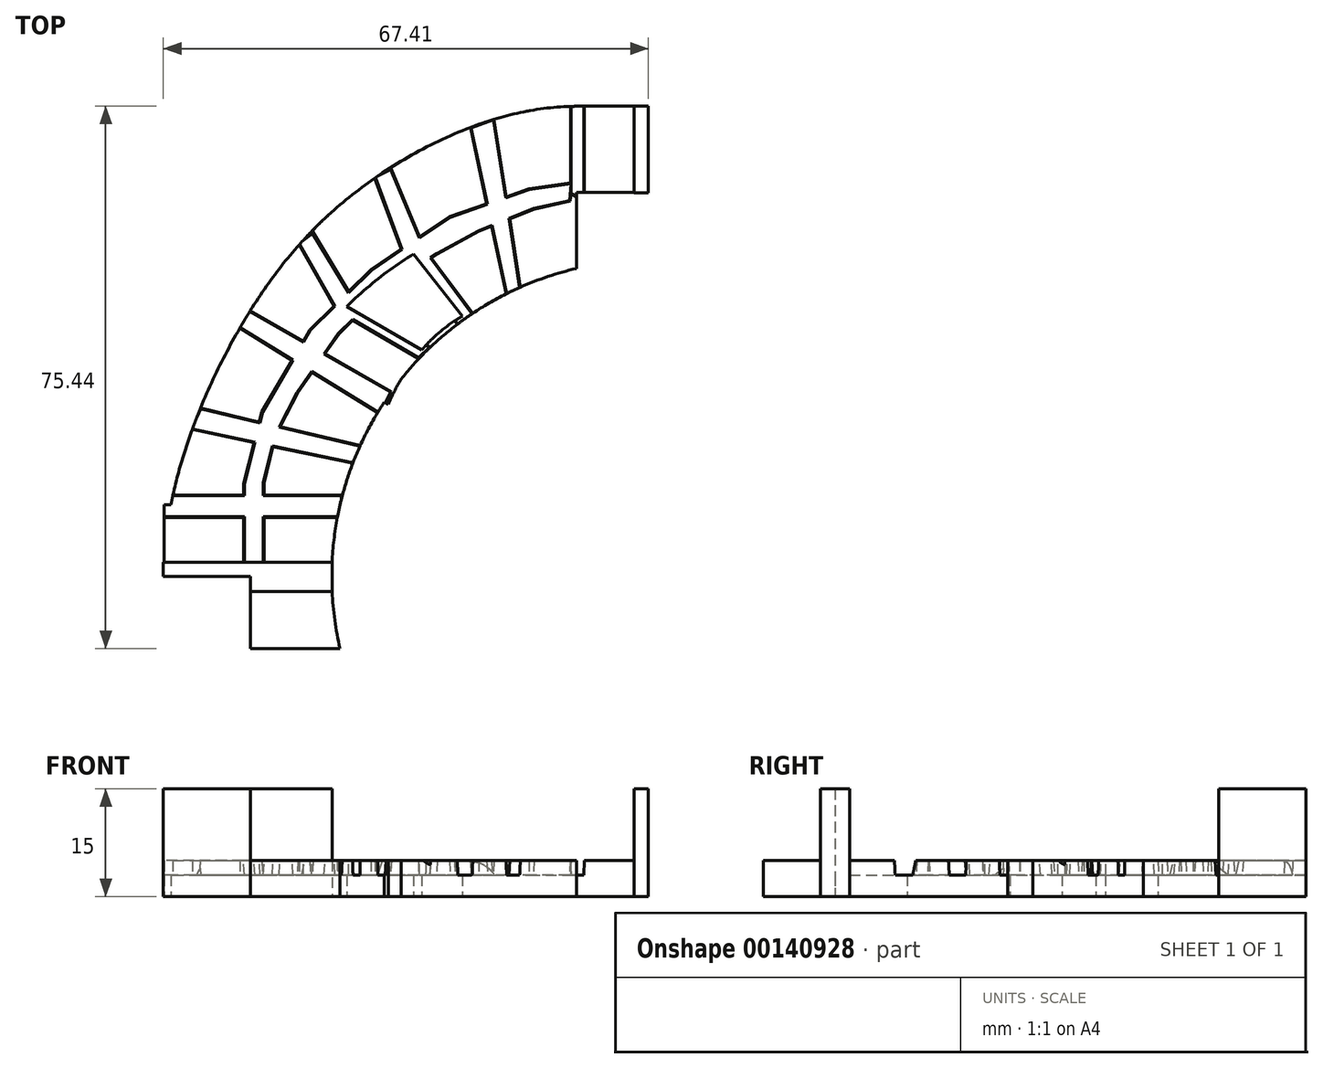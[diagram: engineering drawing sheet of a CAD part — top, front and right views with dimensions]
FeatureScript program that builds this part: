
annotation { "Feature Type Name" : "Feature", "Feature Type Description" : "" }
export const myFeature = defineFeature(function(context is Context, id is Id, definition is map)
    precondition{}
    {
        {
            var Q0;
            Q0=qCreatedBy(makeId("Top.planeOp"),FACE);
            var sketch = newSketch(context, id + "F0", { "sketchPlane" : qUnion([Q0])});
            skLineSegment(sketch, "E0", {"start": v(-44, 0) * mm, "end": v(-55.3, 0) * mm});
            skLineSegment(sketch, "E1.bottom", {"start": v(-55.3, 0) * mm, "end": v(-44, 0) * mm});
            skLineSegment(sketch, "E1.top", {"start": v(-55.3, 10) * mm, "end": v(-42.85, 10) * mm});
            skLineSegment(sketch, "E1.left", {"start": v(-55.3, 0) * mm, "end": v(-55.3, 10) * mm});
            skLineSegment(sketch, "E1.right", {"start": v(-40, 0) * mm, "end": v(-40, 0) * mm});
            skLineSegment(sketch, "E2.bottom", {"start": v(0, 53.4) * mm, "end": v(-10, 53.4) * mm});
            skLineSegment(sketch, "E2.right", {"start": v(-10, 53.4) * mm, "end": v(-10, 42.85) * mm});
            skLineSegment(sketch, "E3.bottom", {"start": v(-55.3, 10) * mm, "end": v(-67.3, 10) * mm});
            skLineSegment(sketch, "E3.top", {"start": v(-55.3, 0) * mm, "end": v(-67.3, 0) * mm});
            skLineSegment(sketch, "E3.left", {"start": v(-55.3, 10) * mm, "end": v(-55.3, 0) * mm});
            skLineSegment(sketch, "E3.right", {"start": v(-67.3, 10) * mm, "end": v(-67.3, 0) * mm});
            skLineSegment(sketch, "E4.bottom", {"start": v(-10, 53.4) * mm, "end": v(0, 53.4) * mm});
            skLineSegment(sketch, "E4.top", {"start": v(-10, 65.4) * mm, "end": v(0, 65.4) * mm});
            skLineSegment(sketch, "E4.left", {"start": v(-10, 53.4) * mm, "end": v(-10, 65.4) * mm});
            skLineSegment(sketch, "E4.right", {"start": v(0, 53.4) * mm, "end": v(0, 65.4) * mm});
            skFitSpline(sketch, "E5", {"points": [v(-67.3, 0) * mm, v(-56.1, 35.7) * mm, v(-37.14, 56.01) * mm, v(-10, 65.4) * mm], "startDerivative": vector(-1.94, 97.4) * mm, "endDerivative": vector(89.19, 0.31) * mm});
            skFitSpline(sketch, "E6", {"points": [v(-55.3, 10) * mm, v(-43.15, 36.3) * mm, v(-25.7, 48.72) * mm, v(-10, 53.4) * mm], "startDerivative": vector(1.43, 78.12) * mm, "endDerivative": vector(52.36, -0.95) * mm});
            skLineSegment(sketch, "E7", {"start": v(-20.71, 51) * mm, "end": v(-18.75, 39.8) * mm});
            skLineSegment(sketch, "E8", {"start": v(-25.83, 36.23) * mm, "end": v(-32.62, 44.89) * mm});
            skLineSegment(sketch, "E9", {"start": v(-31.47, 31.55) * mm, "end": v(-41.92, 37.56) * mm});
            skLineSegment(sketch, "E10", {"start": v(-47.77, 30.64) * mm, "end": v(-36.16, 23.96) * mm});
            skLineSegment(sketch, "E11", {"start": v(-40.58, 17) * mm, "end": v(-55.12, 19.97) * mm});
            skLineSegment(sketch, "E12", {"start": v(-20.71, 51) * mm, "end": v(-22.71, 63.18) * mm});
            skLineSegment(sketch, "E13", {"start": v(-55.12, 19.97) * mm, "end": v(-62.99, 21.58) * mm});
            skLineSegment(sketch, "E14", {"start": v(-47.77, 30.64) * mm, "end": v(-56.1, 35.7) * mm});
            skLineSegment(sketch, "E15", {"start": v(-32.62, 44.89) * mm, "end": v(-37.14, 56.01) * mm});
            skLineSegment(sketch, "E16", {"start": v(-41.92, 37.56) * mm, "end": v(-47.65, 47.1) * mm});
            skLineSegment(sketch, "E17.bottom", {"start": v(-67.3, 0) * mm, "end": v(-44, 0) * mm});
            skLineSegment(sketch, "E17.top", {"start": v(-67.3, 2) * mm, "end": v(-43.95, 2) * mm});
            skLineSegment(sketch, "E17.left", {"start": v(-67.3, 0) * mm, "end": v(-67.3, 2) * mm});
            skLineSegment(sketch, "E18.top", {"start": v(-55.3, -2) * mm, "end": v(-43.95, -2) * mm});
            skLineSegment(sketch, "E19.top", {"start": v(-55.3, -10) * mm, "end": v(-42.85, -10) * mm});
            skLineSegment(sketch, "E19.left", {"start": v(-55.3, 0) * mm, "end": v(-55.3, -10) * mm});
            skLineSegment(sketch, "E20.bottom", {"start": v(0, 65.4) * mm, "end": v(-2, 65.4) * mm});
            skLineSegment(sketch, "E20.left", {"start": v(0, 65.4) * mm, "end": v(0, 53.4) * mm});
            skLineSegment(sketch, "E20.right", {"start": v(-2, 65.4) * mm, "end": v(-2, 53.4) * mm});
            skPoint(sketch, "E21.top.end.orphan", {"position": v(2, 40) * mm});
            skPoint(sketch, "E22", {"position": v(-55.3, -2) * mm});
            skArc(sketch, "E23", {"start": v(-10, 42.85) * mm, "mid": v(-37.37, 23.23) * mm, "end": v(-42.85, -10) * mm});
            skFitSpline(sketch, "E24.trimOffspring", {"points": [v(-40, 0) * mm, v(-37.14, 21.48) * mm, v(-25.7, 36.3) * mm, v(0, 40) * mm], "startDerivative": vector(0, 72.34) * mm, "endDerivative": vector(82.88, 0) * mm});
            skLineSegment(sketch, "E25.trimOffspring", {"start": v(-40, 0) * mm, "end": v(-39.99, 0) * mm});
            skPoint(sketch, "E26.orphan", {"position": v(-39.99, -2) * mm});
            skPoint(sketch, "E27.orphan", {"position": v(-39.99, -10) * mm});
            skSolve(sketch);
        }
        {
            var Q0;
            Q0=qCreatedBy(makeId("Top.planeOp"),FACE);
            cPlane(context, id + "F1", {"entities" : qUnion([Q0]), "cplaneType" : CPlaneType.OFFSET, "offset" : 3 * mm, "width" : 150 * mm, "height" : 150 * mm});
        }
        {
            var Q0;
            Q0=qCreatedBy(id+"F1.planeOp",FACE);
            var sketch = newSketch(context, id + "F2", { "sketchPlane" : qUnion([Q0])});
            skLineSegment(sketch, "E28.bottom", {"start": v(-67.6, 8.33) * mm, "end": v(-42.66, 8.33) * mm});
            skLineSegment(sketch, "E28.top", {"start": v(-67.6, 11.24) * mm, "end": v(-42.66, 11.24) * mm});
            skLineSegment(sketch, "E28.left", {"start": v(-67.6, 8.33) * mm, "end": v(-67.6, 11.24) * mm});
            skLineSegment(sketch, "E28.right", {"start": v(-42.66, 8.33) * mm, "end": v(-42.66, 11.24) * mm});
            skLineSegment(sketch, "E29", {"start": v(-63.47, 20.57) * mm, "end": v(-40.98, 15.83) * mm});
            skLineSegment(sketch, "E30", {"start": v(-40.98, 15.83) * mm, "end": v(-40.06, 18.12) * mm});
            skLineSegment(sketch, "E31", {"start": v(-40.06, 18.12) * mm, "end": v(-62.25, 23.32) * mm});
            skLineSegment(sketch, "E32", {"start": v(-62.25, 23.32) * mm, "end": v(-63.47, 20.57) * mm});
            skLineSegment(sketch, "E33", {"start": v(-56.77, 34.65) * mm, "end": v(-37.27, 22.7) * mm});
            skLineSegment(sketch, "E34", {"start": v(-37.27, 22.7) * mm, "end": v(-35.84, 25.66) * mm});
            skLineSegment(sketch, "E35", {"start": v(-35.84, 25.66) * mm, "end": v(-55.45, 36.9) * mm});
            skLineSegment(sketch, "E36", {"start": v(-55.45, 36.9) * mm, "end": v(-56.77, 34.65) * mm});
            skLineSegment(sketch, "E37", {"start": v(-48.5, 46.29) * mm, "end": v(-43.2, 37) * mm});
            skLineSegment(sketch, "E38", {"start": v(-43.2, 37) * mm, "end": v(-31.96, 30.46) * mm});
            skLineSegment(sketch, "E39", {"start": v(-31.96, 30.46) * mm, "end": v(-30.43, 31.9) * mm});
            skLineSegment(sketch, "E40", {"start": v(-30.43, 31.9) * mm, "end": v(-40.74, 37.92) * mm});
            skLineSegment(sketch, "E41", {"start": v(-40.74, 37.92) * mm, "end": v(-46.66, 47.72) * mm});
            skLineSegment(sketch, "E42", {"start": v(-46.66, 47.72) * mm, "end": v(-48.5, 46.29) * mm});
            skLineSegment(sketch, "E43", {"start": v(-37.94, 55.53) * mm, "end": v(-33.73, 44.18) * mm});
            skLineSegment(sketch, "E44", {"start": v(-33.73, 44.18) * mm, "end": v(-26.43, 35.1) * mm});
            skLineSegment(sketch, "E45", {"start": v(-26.43, 35.1) * mm, "end": v(-24.49, 36.56) * mm});
            skLineSegment(sketch, "E46", {"start": v(-24.49, 36.56) * mm, "end": v(-31.14, 45.43) * mm});
            skLineSegment(sketch, "E47", {"start": v(-31.14, 45.43) * mm, "end": v(-35.84, 56.58) * mm});
            skLineSegment(sketch, "E48", {"start": v(-35.84, 56.58) * mm, "end": v(-37.94, 55.53) * mm});
            skLineSegment(sketch, "E49", {"start": v(-19.63, 39.08) * mm, "end": v(-24.61, 62.41) * mm});
            skLineSegment(sketch, "E50", {"start": v(-24.61, 62.41) * mm, "end": v(-21.55, 63.54) * mm});
            skLineSegment(sketch, "E51", {"start": v(-21.55, 63.54) * mm, "end": v(-17.87, 40.15) * mm});
            skLineSegment(sketch, "E52", {"start": v(-17.87, 40.15) * mm, "end": v(-19.63, 39.08) * mm});
            skLineSegment(sketch, "E53", {"start": v(-10.72, 53.32) * mm, "end": v(-10.72, 65.48) * mm});
            skLineSegment(sketch, "E54", {"start": v(-10.72, 65.48) * mm, "end": v(-8.99, 65.48) * mm});
            skLineSegment(sketch, "E55", {"start": v(-8.99, 65.48) * mm, "end": v(-8.99, 52.4) * mm});
            skLineSegment(sketch, "E56", {"start": v(-8.99, 52.4) * mm, "end": v(-10.72, 53.32) * mm});
            skLineSegment(sketch, "E57", {"start": v(-56.17, 0) * mm, "end": v(-56.17, 12.88) * mm});
            skLineSegment(sketch, "E58", {"start": v(-56.17, 12.88) * mm, "end": v(-53.61, 22.9) * mm});
            skLineSegment(sketch, "E59", {"start": v(-53.61, 22.9) * mm, "end": v(-46.98, 34.23) * mm});
            skLineSegment(sketch, "E60", {"start": v(-46.98, 34.23) * mm, "end": v(-38.5, 42.6) * mm});
            skLineSegment(sketch, "E61", {"start": v(-38.5, 42.6) * mm, "end": v(-27.57, 49.95) * mm});
            skLineSegment(sketch, "E62", {"start": v(-27.57, 49.95) * mm, "end": v(-16.54, 53.83) * mm});
            skLineSegment(sketch, "E63", {"start": v(-16.54, 53.83) * mm, "end": v(-10.72, 54.65) * mm});
            skLineSegment(sketch, "E64", {"start": v(-10.72, 54.65) * mm, "end": v(-10.93, 52.3) * mm});
            skLineSegment(sketch, "E65", {"start": v(-10.93, 52.3) * mm, "end": v(-15.93, 51.18) * mm});
            skLineSegment(sketch, "E66", {"start": v(-15.93, 51.18) * mm, "end": v(-23.6, 48.12) * mm});
            skLineSegment(sketch, "E67", {"start": v(-23.6, 48.12) * mm, "end": v(-29.41, 44.95) * mm});
            skLineSegment(sketch, "E68", {"start": v(-29.41, 44.95) * mm, "end": v(-36.46, 40.25) * mm});
            skLineSegment(sketch, "E69", {"start": v(-36.46, 40.25) * mm, "end": v(-43.1, 33.82) * mm});
            skLineSegment(sketch, "E70", {"start": v(-43.1, 33.82) * mm, "end": v(-48.81, 25.65) * mm});
            skLineSegment(sketch, "E71", {"start": v(-48.81, 25.65) * mm, "end": v(-51.88, 19.73) * mm});
            skLineSegment(sketch, "E72", {"start": v(-51.88, 19.73) * mm, "end": v(-53.51, 13.09) * mm});
            skLineSegment(sketch, "E73", {"start": v(-53.51, 13.09) * mm, "end": v(-53.51, 0) * mm});
            skLineSegment(sketch, "E74", {"start": v(-53.51, 0) * mm, "end": v(-56.17, 0) * mm});
            skSolve(sketch);
        }
        {
            var Q0;
            Q0 = qSketchRegion(id + "F0", true);
            var Q1;
            {var subQ0=sQuery(id+"F0.wireOp",EDGE,"E3.bottom");Q1=makeQuery(id+"F0.imprint","IMPRINT",FACE,{"disambiguationData":[TD([[makeQuery(id+"F0.imprint","IMPRINT",EDGE,{"derivedFrom":subQ0}),1.0]])]});}
            var Q2;
            {var subQ0=sQuery(id+"F0.wireOp",EDGE,"E1.top");Q2=makeQuery(id+"F0.imprint","IMPRINT",FACE,{"disambiguationData":[TD([[makeQuery(id+"F0.imprint","IMPRINT",EDGE,{"derivedFrom":subQ0}),-1.0]])]});}
            extrude(context, id + "F3", {"entities" : qUnion([Q0, Q1, Q2]), "depth" : 5 * mm});
        }
        {
            var Q0;
            Q0 = qSketchRegion(id + "F2", true);
            extrude(context, id + "F4", {"entities" : qUnion([Q0]), "operationType" : NewBodyOperationType.REMOVE, "depth" : 25 * mm, "hasDraft" : true, "draftAngle" : 3 * degree});
        }
        {
            var Q0;
            Q0=qCreatedBy(makeId("Top.planeOp"),FACE);
            var sketch = newSketch(context, id + "F5", { "sketchPlane" : qUnion([Q0])});
            skLineSegment(sketch, "E75.bottom", {"start": v(0, 65.44) * mm, "end": v(-1.96, 65.44) * mm});
            skLineSegment(sketch, "E75.top", {"start": v(0, 53.34) * mm, "end": v(-1.96, 53.34) * mm});
            skLineSegment(sketch, "E75.left", {"start": v(0, 65.44) * mm, "end": v(0, 53.34) * mm});
            skLineSegment(sketch, "E75.right", {"start": v(-1.96, 65.44) * mm, "end": v(-1.96, 53.34) * mm});
            skLineSegment(sketch, "E76.bottom", {"start": v(-67.4, 0) * mm, "end": v(-43.92, 0) * mm});
            skLineSegment(sketch, "E76.top", {"start": v(-67.4, 1.98) * mm, "end": v(-43.92, 1.98) * mm});
            skLineSegment(sketch, "E76.left", {"start": v(-67.4, 0) * mm, "end": v(-67.4, 1.98) * mm});
            skLineSegment(sketch, "E76.right", {"start": v(-43.92, 0) * mm, "end": v(-43.92, 1.98) * mm});
            skLineSegment(sketch, "E77.bottom", {"start": v(-55.3, 0) * mm, "end": v(-43.92, 0) * mm});
            skLineSegment(sketch, "E77.top", {"start": v(-55.3, -2.07) * mm, "end": v(-43.92, -2.07) * mm});
            skLineSegment(sketch, "E77.right", {"start": v(-43.92, 0) * mm, "end": v(-43.92, -2.07) * mm});
            skLineSegment(sketch, "E78", {"start": v(-55.3, 0) * mm, "end": v(-55.3, -2.07) * mm});
            skPoint(sketch, "E79.orphan", {"position": v(-55.67, 0) * mm});
            skSolve(sketch);
        }
        {
            var Q0;
            Q0 = qSketchRegion(id + "F5", true);
            extrude(context, id + "F6", {"entities" : qUnion([Q0]), "operationType" : NewBodyOperationType.ADD, "depth" : 15 * mm});
        }
    });
